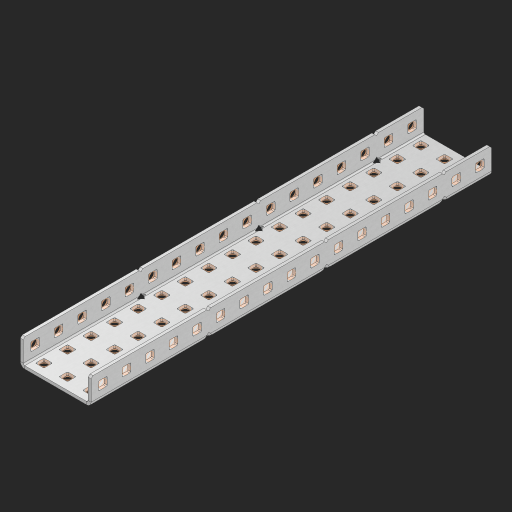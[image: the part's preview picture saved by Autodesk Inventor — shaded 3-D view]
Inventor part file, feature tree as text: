
AUTODESK INVENTOR PART (.ipt)
format: ipt  version: 2023 (Build 270158000, 158)  size: 1,245,184 bytes
history: native  units: in
note: dims shown in document units (in); Inventor stores cm internally (conversion verified against a paired STEP export)
features: other x90, extrude x84, sheet_metal_op x10, sketch x8, mirror x1, pattern_linear x1, chamfer x1
ambient origin geometry x8: Origin, YZ Plane, XZ Plane, XY Plane, X Axis, Y Axis, Z Axis, Center Point
bodies: Solid1 (feature_tree), Body (feature_tree)
feature tree (195):
  other  "Flange Pattern Plane"
  sheet_metal_op  "Flange Pattern"
  sheet_metal_op  "Body Pattern"
  other  "Arc Length"
  mirror  "Notch Mirror"
  pattern_linear  "Notch Pattern"  Spacing1=0.25in  [1 undecoded]
  chamfer  "End Chamfer"
  extrude  "Half Cut"  Depth=0.0625in
  sketch  "Sketch1"  dims[d0=1.5in]
  other  "Plate1"
  sketch  "Sketch2"  dims[d1=8.5in]
  other  "Plate2"
  sheet_metal_op  "Bend1"
  sheet_metal_op  "Corner1"
  sketch  "Sketch3"  dims[d2=0.0625in]
  other  "Flange Pattern Sketch"
  sketch  "Sketch7"  dims[d3=0.0625in]
  other  "Srf1"
  other  "Srf2"
  sketch  "Sketch8"  dims[d4=0.0312in]
  sketch  "Sketch9"  dims[d5=0.125in]
  other  "Srf91"
  sheet_metal_op  "Body Pattern Sketch"
  other  "Srf92"
  sketch  "Sketch13"  dims[d6=0.0625in]
  sketch  "Sketch14"  dims[d7=0.5in d8=90.0deg d9=0.0312in d10=0.25in d11=0.0625in d12=0.0625in d16=0.182in d17=0.02in d18=0.0625in d19=0.0in d20=0.25in d21=0.25in d46=0.172in d47=1.0in d48=0.0in d49=0.182in d50=0.02in d51=0.25in d52=0.25in d53=0.0625in d54=0.0in d55=0.172in d56=1.0in d57=0.0in d60=6.6929in d62=0.5in d63=1.1811in d65=0.5in d85=0.1473in d86=0.1782in d88=0.04in d89=0.0625in d90=0.0in d91=0.04in d92=0.0491in d95=2.5in d96=0.04in d97=0.25in d98=45.0deg d101=0.0in d102=2.497in d131=1.5in d132=6.6929in d134=0.5in d139=0.5in]
  other  "Srf856"
  other  "Srf1310"
  other  "Srf1311"
  other  "Srf1312"
  other  "Srf1376"
  other  "Srf1377"
  other  "Srf1728"
  other  "Srf1755"
  other  "Srf1878"
  other  "Srf1879"
  other  "Srf1880"
  other  "Srf1881"
  other  "Srf1882"
  other  "Srf1883"
  other  "Srf1884"
  other  "Srf1885"
  other  "Srf1886"
  other  "Srf1887"
  other  "Srf1888"
  other  "Srf1889"
  other  "Srf1890"
  other  "Srf1891"
  other  "Srf1892"
  other  "Srf1893"
  other  "Srf1894"
  other  "Srf1895"
  other  "Srf1896"
  other  "Srf1897"
  other  "Srf1898"
  other  "Srf1899"
  other  "Srf1900"
  other  "Srf1901"
  other  "Srf1902"
  other  "Srf1903"
  other  "Srf1904"
  other  "Srf1905"
  other  "Srf1942"
  other  "Srf1943"
  other  "Srf1944"
  other  "Srf1945"
  other  "Srf1946"
  other  "Srf1947"
  other  "Srf1948"
  other  "Srf1949"
  other  "Srf1950"
  other  "Srf1951"
  other  "Srf1952"
  other  "Srf1953"
  other  "Srf1954"
  other  "Srf1955"
  other  "Srf1956"
  other  "Srf1957"
  other  "Srf1958"
  other  "Srf1959"
  other  "Srf1960"
  other  "Srf1961"
  other  "Srf1962"
  other  "Srf1963"
  other  "Srf1964"
  other  "Srf1965"
  other  "Srf1966"
  other  "Srf1967"
  other  "Srf1968"
  other  "Srf1969"
  other  "Srf1970"
  other  "Srf1971"
  other  "Srf1972"
  other  "Srf1973"
  other  "Srf1974"
  other  "Srf1975"
  other  "Srf1976"
  other  "Srf1977"
  other  "Srf1978"
  other  "Srf1979"
  other  "Srf1980"
  other  "Srf1981"
  other  "Srf1982"
  other  "Srf1983"
  other  "Srf1984"
  other  "Srf1985"
  other  "Srf1986"
  sheet_metal_op  "Flange Stamp"
  sheet_metal_op  "Flange Circle"
  sheet_metal_op  "Body Stamp"
  sheet_metal_op  "Body Circle"
  sheet_metal_op  "Notch"
  extrude  "ExtrusionSrf2"  Depth=0.0625in
  extrude  "ExtrusionSrf92"  Depth=1.5in
  extrude  "ExtrusionSrf856"  Depth=0.02in
  extrude  "ExtrusionSrf1310"  Depth=0.0625in
  extrude  "ExtrusionSrf1311"  TaperAngle=0.0deg  [1 undecoded]
  extrude  "ExtrusionSrf1312"  Depth=0.25in
  extrude  "ExtrusionSrf1376"  Depth=0.25in
  extrude  "ExtrusionSrf1377"  Depth=1.5in
  extrude  "ExtrusionSrf1728"  Depth=1.5in TaperAngle=0.0deg
  extrude  "ExtrusionSrf1755"  Depth=1.5in
  extrude  "ExtrusionSrf1878"  Depth=0.02in
  extrude  "ExtrusionSrf1879"  Depth=0.25in
  extrude  "ExtrusionSrf1880"  Depth=0.25in
  extrude  "ExtrusionSrf1881"  Depth=0.0625in
  extrude  "ExtrusionSrf1882"  TaperAngle=0.0deg  [1 undecoded]
  extrude  "ExtrusionSrf1883"  Depth=1.5in
  extrude  "ExtrusionSrf1884"  Depth=1.5in TaperAngle=0.0deg
  extrude  "ExtrusionSrf1885"  Depth=1.5in
  extrude  "ExtrusionSrf1886"  Depth=1.5in
  extrude  "ExtrusionSrf1887"  Depth=1.5in
  extrude  "ExtrusionSrf1888"  Depth=1.5in
  extrude  "ExtrusionSrf1889"  Depth=1.5in
  extrude  "ExtrusionSrf1890"  Depth=0.0625in
  extrude  "ExtrusionSrf1891"  TaperAngle=0.0deg  [1 undecoded]
  extrude  "ExtrusionSrf1892"  Depth=1.5in
  extrude  "ExtrusionSrf1893"  Depth=1.5in
  extrude  "ExtrusionSrf1894"  Depth=1.5in
  extrude  "ExtrusionSrf1895"  Depth=0.25in TaperAngle=45.0deg
  extrude  "ExtrusionSrf1896"  TaperAngle=0.0deg  [1 undecoded]
  extrude  "ExtrusionSrf1897"  Depth=1.5in
  extrude  "ExtrusionSrf1898"  Depth=1.5in
  extrude  "ExtrusionSrf1899"  Depth=1.5in
  extrude  "ExtrusionSrf1900"  Depth=1.5in
  extrude  "ExtrusionSrf1901"  Depth=1.5in
  extrude  "ExtrusionSrf1902"  [1 undecoded]
  extrude  "ExtrusionSrf1903"  [1 undecoded]
  extrude  "ExtrusionSrf1904"  [1 undecoded]
  extrude  "ExtrusionSrf1905"  [1 undecoded]
  extrude  "ExtrusionSrf1942"  [1 undecoded]
  extrude  "ExtrusionSrf1943"  [1 undecoded]
  extrude  "ExtrusionSrf1944"  [1 undecoded]
  extrude  "ExtrusionSrf1945"  [1 undecoded]
  extrude  "ExtrusionSrf1946"  [1 undecoded]
  extrude  "ExtrusionSrf1947"  [1 undecoded]
  extrude  "ExtrusionSrf1948"  [1 undecoded]
  extrude  "ExtrusionSrf1949"  [1 undecoded]
  extrude  "ExtrusionSrf1950"  [1 undecoded]
  extrude  "ExtrusionSrf1951"  [1 undecoded]
  extrude  "ExtrusionSrf1952"  [1 undecoded]
  extrude  "ExtrusionSrf1953"  [1 undecoded]
  extrude  "ExtrusionSrf1954"  [1 undecoded]
  extrude  "ExtrusionSrf1955"  [1 undecoded]
  extrude  "ExtrusionSrf1956"  [1 undecoded]
  extrude  "ExtrusionSrf1957"  [1 undecoded]
  extrude  "ExtrusionSrf1958"  [1 undecoded]
  extrude  "ExtrusionSrf1959"  [1 undecoded]
  extrude  "ExtrusionSrf1960"  [1 undecoded]
  extrude  "ExtrusionSrf1961"  [1 undecoded]
  extrude  "ExtrusionSrf1962"  [1 undecoded]
  extrude  "ExtrusionSrf1963"  [1 undecoded]
  extrude  "ExtrusionSrf1964"  [1 undecoded]
  extrude  "ExtrusionSrf1965"  [1 undecoded]
  extrude  "ExtrusionSrf1966"  [1 undecoded]
  extrude  "ExtrusionSrf1967"  [1 undecoded]
  extrude  "ExtrusionSrf1968"  [1 undecoded]
  extrude  "ExtrusionSrf1969"  [1 undecoded]
  extrude  "ExtrusionSrf1970"  [1 undecoded]
  extrude  "ExtrusionSrf1971"  [1 undecoded]
  extrude  "ExtrusionSrf1972"  [1 undecoded]
  extrude  "ExtrusionSrf1973"  [1 undecoded]
  extrude  "ExtrusionSrf1974"  [1 undecoded]
  extrude  "ExtrusionSrf1975"  [1 undecoded]
  extrude  "ExtrusionSrf1976"  [1 undecoded]
  extrude  "ExtrusionSrf1977"  [1 undecoded]
  extrude  "ExtrusionSrf1978"  [1 undecoded]
  extrude  "ExtrusionSrf1979"  [1 undecoded]
  extrude  "ExtrusionSrf1980"  [1 undecoded]
  extrude  "ExtrusionSrf1981"  [1 undecoded]
  extrude  "ExtrusionSrf1982"  [1 undecoded]
  extrude  "ExtrusionSrf1983"  [1 undecoded]
  extrude  "ExtrusionSrf1984"  [1 undecoded]
  extrude  "ExtrusionSrf1985"  [1 undecoded]
  extrude  "ExtrusionSrf1986"  [1 undecoded]
note: 54 required parameter values undecoded (feature->parameter linkage not recoverable at this tier; creation-order binding heuristic only, values carry confidence <= 0.55)
